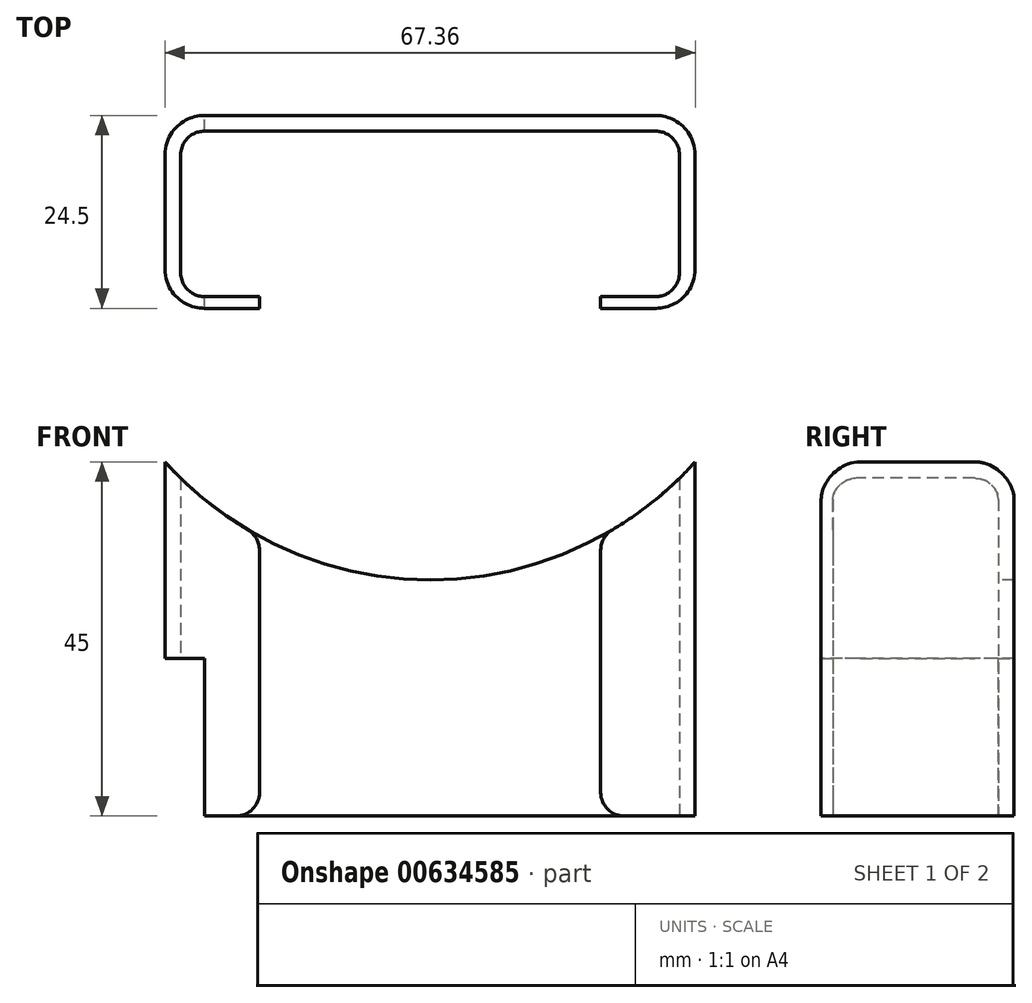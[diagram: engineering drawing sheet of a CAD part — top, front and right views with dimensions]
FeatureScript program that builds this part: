
annotation { "Feature Type Name" : "Feature", "Feature Type Description" : "" }
export const myFeature = defineFeature(function(context is Context, id is Id, definition is map)
    precondition{}
    {
        {
            var Q0;
            Q0=qCreatedBy(makeId("Top.planeOp"),FACE);
            var sketch = newSketch(context, id + "F0", { "sketchPlane" : qUnion([Q0])});
            skPoint(sketch, "E0.middle", {"position": v(0, 0) * mm});
            skLineSegment(sketch, "E1.bottom", {"start": v(28.68, 10.5) * mm, "end": v(-28.68, 10.5) * mm});
            skLineSegment(sketch, "E1.top", {"start": v(28.68, -10.5) * mm, "end": v(21.68, -10.5) * mm});
            skLineSegment(sketch, "E1.left", {"start": v(31.68, 7.5) * mm, "end": v(31.68, -7.5) * mm});
            skLineSegment(sketch, "E1.right", {"start": v(-31.68, 7.5) * mm, "end": v(-31.68, -7.5) * mm});
            skLineSegment(sketch, "E2", {"start": v(21.68, -10.5) * mm, "end": v(21.68, -12) * mm});
            skLineSegment(sketch, "E3.trimOffspring", {"start": v(-21.68, -10.5) * mm, "end": v(-28.68, -10.5) * mm});
            skPoint(sketch, "E4.visualSharp", {"position": v(-31.68, 10.5) * mm});
            skArc(sketch, "E4.filletArc", {"start": v(-28.68, 10.5) * mm, "mid": v(-30.8, 9.62) * mm, "end": v(-31.68, 7.5) * mm});
            skPoint(sketch, "E5.visualSharp", {"position": v(31.68, 10.5) * mm});
            skArc(sketch, "E5.filletArc", {"start": v(31.68, 7.5) * mm, "mid": v(30.8, 9.62) * mm, "end": v(28.68, 10.5) * mm});
            skPoint(sketch, "E6.visualSharp", {"position": v(31.68, -10.5) * mm});
            skArc(sketch, "E6.filletArc", {"start": v(28.68, -10.5) * mm, "mid": v(30.8, -9.62) * mm, "end": v(31.68, -7.5) * mm});
            skPoint(sketch, "E7.visualSharp", {"position": v(-31.68, -10.5) * mm});
            skArc(sketch, "E7.filletArc", {"start": v(-31.68, -7.5) * mm, "mid": v(-30.8, -9.62) * mm, "end": v(-28.68, -10.5) * mm});
            skLineSegment(sketch, "E8", {"start": v(-21.68, -12) * mm, "end": v(-28.67, -12) * mm});
            skLineSegment(sketch, "E9", {"start": v(-21.68, -10.5) * mm, "end": v(-21.68, -12) * mm});
            skLineSegment(sketch, "E10", {"start": v(-33.68, -7) * mm, "end": v(-33.68, 7.5) * mm});
            skLineSegment(sketch, "E11", {"start": v(-28.68, 12.5) * mm, "end": v(28.68, 12.5) * mm});
            skLineSegment(sketch, "E12", {"start": v(33.68, 7.5) * mm, "end": v(33.68, -7) * mm});
            skLineSegment(sketch, "E13", {"start": v(21.68, -12) * mm, "end": v(28.67, -12) * mm});
            skPoint(sketch, "E14.visualSharp", {"position": v(-33.68, 12.5) * mm});
            skArc(sketch, "E14.filletArc", {"start": v(-28.68, 12.5) * mm, "mid": v(-32.21, 11.04) * mm, "end": v(-33.68, 7.5) * mm});
            skPoint(sketch, "E15.visualSharp", {"position": v(33.68, 12.5) * mm});
            skArc(sketch, "E15.filletArc", {"start": v(33.68, 7.5) * mm, "mid": v(32.21, 11.04) * mm, "end": v(28.68, 12.5) * mm});
            skPoint(sketch, "E16.visualSharp", {"position": v(33.68, -12) * mm});
            skArc(sketch, "E16.filletArc", {"start": v(28.67, -12) * mm, "mid": v(32.21, -10.54) * mm, "end": v(33.68, -7) * mm});
            skPoint(sketch, "E17.visualSharp", {"position": v(-33.68, -12) * mm});
            skArc(sketch, "E17.filletArc", {"start": v(-33.68, -7) * mm, "mid": v(-32.21, -10.54) * mm, "end": v(-28.67, -12) * mm});
            skSolve(sketch);
        }
        {
            var Q0;
            Q0 = qSketchRegion(id + "F0", true);
            extrude(context, id + "F1", {"entities" : qUnion([Q0]), "depth" : 45 * mm, "offsetDistance" : 25 * mm});
        }
        {
            var Q0;
            Q0=qCreatedBy(makeId("Front.planeOp"),FACE);
            var sketch = newSketch(context, id + "F2", { "sketchPlane" : qUnion([Q0])});
            skLineSegment(sketch, "E18", {"start": v(33.68, 45) * mm, "end": v(-33.68, 45) * mm});
            skArc(sketch, "E19", {"start": v(-33.68, 45) * mm, "mid": v(0, 30) * mm, "end": v(33.68, 45) * mm});
            skSolve(sketch);
        }
        {
            var Q0;
            Q0 = qSketchRegion(id + "F2", true);
            extrude(context, id + "F3", {"entities" : qUnion([Q0]), "operationType" : NewBodyOperationType.REMOVE, "endBound" : BoundingType.SYMMETRIC, "oppositeDirection" : true, "depth" : 50 * mm, "offsetDistance" : 25 * mm});
        }
        {
            var Q0;
            Q0=makeQuery(id+"F1.opExtrude","SWEPT_FACE",FACE,{"disambiguationData":[OSD([sQuery(id+"F0.wireOp",EDGE,"E10")])]});
            var sketch = newSketch(context, id + "F4", { "sketchPlane" : qUnion([Q0])});
            skPoint(sketch, "E20.middle", {"position": v(0, 0) * mm});
            skLineSegment(sketch, "E21.bottom", {"start": v(26.53, 20) * mm, "end": v(-26.53, 20) * mm});
            skLineSegment(sketch, "E21.top", {"start": v(26.53, -20) * mm, "end": v(-26.53, -20) * mm});
            skLineSegment(sketch, "E21.left", {"start": v(26.53, 20) * mm, "end": v(26.53, -20) * mm});
            skLineSegment(sketch, "E21.right", {"start": v(-26.53, 20) * mm, "end": v(-26.53, -20) * mm});
            skSolve(sketch);
        }
        {
            var Q0;
            Q0 = qSketchRegion(id + "F4", true);
            var Q1;
            Q1=makeQuery(id+"F1.opExtrude","SWEPT_FACE",FACE,{"disambiguationData":[OSD([sQuery(id+"F0.wireOp",EDGE,"E1.right")])]});
            var Q2;
            Q2=makeQuery(id+"F1.opExtrude","CAP_VERTEX",VERTEX,{"disambiguationData":[OSD([sQuery(id+"F0.wireOp",EDGE,"E1.bottom"),sQuery(id+"F0.wireOp",EDGE,"E4.filletArc")])],"isStart":true});
            extrude(context, id + "F5", {"entities" : qUnion([Q0]), "operationType" : NewBodyOperationType.REMOVE, "endBound" : BoundingType.UP_TO_VERTEX, "oppositeDirection" : true, "depth" : 25 * mm, "endBoundEntityFace" : qUnion([Q1]), "endBoundEntityVertex" : qUnion([Q2]), "offsetDistance" : 25 * mm});
        }
        {
            var Q0;
            Q0=makeQuery(id+"F5.boolean.opBoolean","INTERSECT",EDGE,{"disambiguationData":[OD(0.0)],"derivedFrom":[makeQuery(id+"F1.opExtrude","CAP_FACE",FACE,{"disambiguationData":[OSD([sQuery(id+"F0.wireOp",EDGE,"E1.bottom"),sQuery(id+"F0.wireOp",EDGE,"E1.top"),sQuery(id+"F0.wireOp",EDGE,"E1.left"),sQuery(id+"F0.wireOp",EDGE,"E1.right"),sQuery(id+"F0.wireOp",EDGE,"E2"),sQuery(id+"F0.wireOp",EDGE,"E3.trimOffspring"),sQuery(id+"F0.wireOp",EDGE,"E4.filletArc"),sQuery(id+"F0.wireOp",EDGE,"E5.filletArc"),sQuery(id+"F0.wireOp",EDGE,"E6.filletArc"),sQuery(id+"F0.wireOp",EDGE,"E7.filletArc"),sQuery(id+"F0.wireOp",EDGE,"E8"),sQuery(id+"F0.wireOp",EDGE,"E9"),sQuery(id+"F0.wireOp",EDGE,"E10"),sQuery(id+"F0.wireOp",EDGE,"E11"),sQuery(id+"F0.wireOp",EDGE,"E12"),sQuery(id+"F0.wireOp",EDGE,"E13"),sQuery(id+"F0.wireOp",EDGE,"E14.filletArc"),sQuery(id+"F0.wireOp",EDGE,"E15.filletArc"),sQuery(id+"F0.wireOp",EDGE,"E16.filletArc"),sQuery(id+"F0.wireOp",EDGE,"E17.filletArc")])],"isStart":true}),makeQuery(id+"F5.opExtrude","CAP_FACE",FACE,{"disambiguationData":[OSD([dummyQuery(id+"F5.vertexPlane.planeOp",FACE)])],"isStart":false})]});
            var Q1;
            Q1=makeQuery(id+"F5.boolean.opBoolean","INTERSECT",EDGE,{"disambiguationData":[OD(1.0)],"derivedFrom":[makeQuery(id+"F1.opExtrude","CAP_FACE",FACE,{"disambiguationData":[OSD([sQuery(id+"F0.wireOp",EDGE,"E1.bottom"),sQuery(id+"F0.wireOp",EDGE,"E1.top"),sQuery(id+"F0.wireOp",EDGE,"E1.left"),sQuery(id+"F0.wireOp",EDGE,"E1.right"),sQuery(id+"F0.wireOp",EDGE,"E2"),sQuery(id+"F0.wireOp",EDGE,"E3.trimOffspring"),sQuery(id+"F0.wireOp",EDGE,"E4.filletArc"),sQuery(id+"F0.wireOp",EDGE,"E5.filletArc"),sQuery(id+"F0.wireOp",EDGE,"E6.filletArc"),sQuery(id+"F0.wireOp",EDGE,"E7.filletArc"),sQuery(id+"F0.wireOp",EDGE,"E8"),sQuery(id+"F0.wireOp",EDGE,"E9"),sQuery(id+"F0.wireOp",EDGE,"E10"),sQuery(id+"F0.wireOp",EDGE,"E11"),sQuery(id+"F0.wireOp",EDGE,"E12"),sQuery(id+"F0.wireOp",EDGE,"E13"),sQuery(id+"F0.wireOp",EDGE,"E14.filletArc"),sQuery(id+"F0.wireOp",EDGE,"E15.filletArc"),sQuery(id+"F0.wireOp",EDGE,"E16.filletArc"),sQuery(id+"F0.wireOp",EDGE,"E17.filletArc")])],"isStart":true}),makeQuery(id+"F5.opExtrude","CAP_FACE",FACE,{"disambiguationData":[OSD([dummyQuery(id+"F5.vertexPlane.planeOp",FACE)])],"isStart":false})]});
            var Q2;
            Q2=makeQuery(id+"F1.opExtrude","CAP_EDGE",EDGE,{"disambiguationData":[OSD([sQuery(id+"F0.wireOp",EDGE,"E9")])],"isStart":true});
            var Q3;
            Q3=makeQuery(id+"F1.opExtrude","CAP_EDGE",EDGE,{"disambiguationData":[OSD([sQuery(id+"F0.wireOp",EDGE,"E2")])],"isStart":true});
            var Q4;
            Q4=makeQuery(id+"F3.boolean.opBoolean","INTERSECT",EDGE,{"derivedFrom":[makeQuery(id+"F1.opExtrude","SWEPT_FACE",FACE,{"disambiguationData":[OSD([sQuery(id+"F0.wireOp",EDGE,"E2")])]}),makeQuery(id+"F3.opExtrude","SWEPT_FACE",FACE,{"disambiguationData":[OSD([sQuery(id+"F2.wireOp",EDGE,"E19")])]})]});
            var Q5;
            Q5=makeQuery(id+"F3.boolean.opBoolean","INTERSECT",EDGE,{"derivedFrom":[makeQuery(id+"F1.opExtrude","SWEPT_FACE",FACE,{"disambiguationData":[OSD([sQuery(id+"F0.wireOp",EDGE,"E9")])]}),makeQuery(id+"F3.opExtrude","SWEPT_FACE",FACE,{"disambiguationData":[OSD([sQuery(id+"F2.wireOp",EDGE,"E19")])]})]});
            fillet(context, id + "F6", {"entities" : qUnion([Q0, Q1, Q2, Q3, Q4, Q5]), "radius" : 3 * mm, "tangentPropagation" : true, "allowEdgeOverflow" : false});
        }
    });
